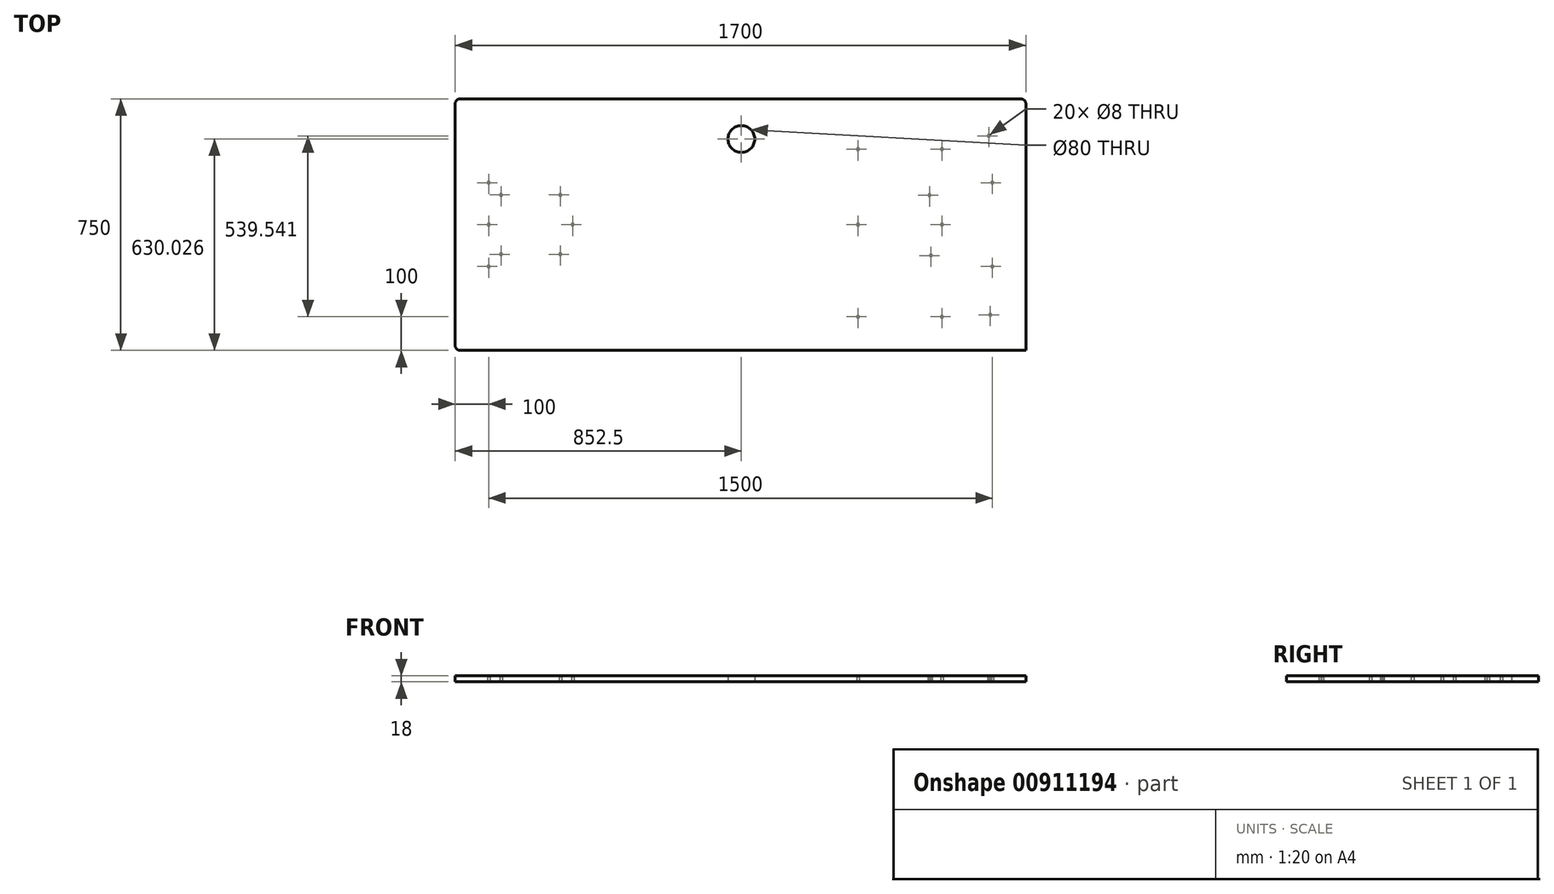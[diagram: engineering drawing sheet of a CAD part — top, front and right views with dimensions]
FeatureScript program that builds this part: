
annotation { "Feature Type Name" : "Feature", "Feature Type Description" : "" }
export const myFeature = defineFeature(function(context is Context, id is Id, definition is map)
    precondition{}
    {
        {
            var Q0;
            Q0=qCreatedBy(makeId("Top.planeOp"),FACE);
            var sketch = newSketch(context, id + "F0", { "sketchPlane" : qUnion([Q0])});
            skLineSegment(sketch, "E0", {"start": v(0, 0) * mm, "end": v(1700, 0) * mm});
            skLineSegment(sketch, "E1", {"start": v(1700, 0) * mm, "end": v(1700, -750) * mm});
            skLineSegment(sketch, "E2", {"start": v(1700, -750) * mm, "end": v(0, -750) * mm});
            skLineSegment(sketch, "E3", {"start": v(0, -750) * mm, "end": v(0, 0) * mm});
            skLineSegment(sketch, "E4", {"start": v(1700, -750) * mm, "end": v(1690, -750) * mm});
            skSolve(sketch);
        }
        {
            var Q0;
            Q0=makeQuery(id+"F0.imprint","IMPRINT",FACE,{"disambiguationData":[TD([[makeQuery(id+"F0.imprint","IMPRINT",EDGE,{"derivedFrom":sQuery(id+"F0.wireOp",EDGE,"E0")}),-1.0]])]});
            extrude(context, id + "F1", {"entities" : qUnion([Q0]), "depth" : 18 * mm, "offsetDistance" : 25 * mm});
        }
        {
            var Q0;
            Q0=makeQuery(id+"F1.opExtrude","SWEPT_EDGE",EDGE,{"disambiguationData":[OSD([sQuery(id+"F0.wireOp",EDGE,"E2"),sQuery(id+"F0.wireOp",EDGE,"E3")])]});
            var Q1;
            Q1=makeQuery(id+"F1.opExtrude","SWEPT_EDGE",EDGE,{"disambiguationData":[OSD([sQuery(id+"F0.wireOp",EDGE,"E0"),sQuery(id+"F0.wireOp",EDGE,"E3")])]});
            var Q2;
            Q2=makeQuery(id+"F1.opExtrude","SWEPT_EDGE",EDGE,{"disambiguationData":[OSD([sQuery(id+"F0.wireOp",EDGE,"E0"),sQuery(id+"F0.wireOp",EDGE,"E1")])]});
            fillet(context, id + "F2", {"entities" : qUnion([Q0, Q1, Q2]), "radius" : 15 * mm, "tangentPropagation" : true, "allowEdgeOverflow" : false});
        }
        {
            var Q0;
            Q0=makeQuery(id+"F1.opExtrude","CAP_FACE",FACE,{"disambiguationData":[OSD([sQuery(id+"F0.wireOp",EDGE,"E0"),sQuery(id+"F0.wireOp",EDGE,"E1"),sQuery(id+"F0.wireOp",EDGE,"E2"),sQuery(id+"F0.wireOp",EDGE,"E3"),sQuery(id+"F0.wireOp",EDGE,"E4")])],"isStart":true});
            var sketch = newSketch(context, id + "F3", { "sketchPlane" : qUnion([Q0])});
            skCircle(sketch, "E5", {"center": v(100, 500) * mm, "radius": 4 * mm});
            skCircle(sketch, "E6", {"center": v(100, 250) * mm, "radius": 4 * mm});
            skCircle(sketch, "E7", {"center": v(100, 375) * mm, "radius": 4 * mm});
            skCircle(sketch, "E8", {"center": v(313.39, 463.39) * mm, "radius": 4 * mm});
            skCircle(sketch, "E9", {"center": v(136.61, 286.61) * mm, "radius": 4 * mm});
            skCircle(sketch, "E10", {"center": v(136.61, 463.39) * mm, "radius": 4 * mm});
            skCircle(sketch, "E11", {"center": v(313.39, 286.61) * mm, "radius": 4 * mm});
            skCircle(sketch, "E12", {"center": v(350, 375) * mm, "radius": 4 * mm});
            skLineSegment(sketch, "E13", {"start": v(1700, 15) * mm, "end": v(1700, 115) * mm});
            skCircle(sketch, "E14", {"center": v(1450, 150) * mm, "radius": 4 * mm});
            skCircle(sketch, "E15", {"center": v(1200, 150) * mm, "radius": 4 * mm});
            skLineSegment(sketch, "E16", {"start": v(1450, 150) * mm, "end": v(1450, 0) * mm});
            skLineSegment(sketch, "E17", {"start": v(1200, 150) * mm, "end": v(1200, 0) * mm});
            skLineSegment(sketch, "E18", {"start": v(1700, 750) * mm, "end": v(1700, 375) * mm});
            skCircle(sketch, "E19", {"center": v(1450, 375) * mm, "radius": 4 * mm});
            skLineSegment(sketch, "E20", {"start": v(1450, 375) * mm, "end": v(1200, 375) * mm});
            skCircle(sketch, "E21", {"center": v(1200, 375) * mm, "radius": 4 * mm});
            skLineSegment(sketch, "E22", {"start": v(1450, 375) * mm, "end": v(1450, 650) * mm});
            skCircle(sketch, "E23", {"center": v(1450, 650) * mm, "radius": 4 * mm});
            skLineSegment(sketch, "E24", {"start": v(1450, 650) * mm, "end": v(1200, 650) * mm});
            skCircle(sketch, "E25", {"center": v(1200, 650) * mm, "radius": 4 * mm});
            skLineSegment(sketch, "E26", {"start": v(1700, 375) * mm, "end": v(1600, 375) * mm});
            skLineSegment(sketch, "E27", {"start": v(1600, 375) * mm, "end": v(1600, 250) * mm});
            skCircle(sketch, "E28", {"center": v(1600, 250) * mm, "radius": 4 * mm});
            skLineSegment(sketch, "E29", {"start": v(1600, 375) * mm, "end": v(1600, 500) * mm});
            skCircle(sketch, "E30", {"center": v(1600, 500) * mm, "radius": 4 * mm});
            skLineSegment(sketch, "E31", {"start": v(1700, 750) * mm, "end": v(1593.93, 643.93) * mm});
            skCircle(sketch, "E32", {"center": v(1593.93, 643.93) * mm, "radius": 4 * mm});
            skLineSegment(sketch, "E33", {"start": v(1593.93, 643.93) * mm, "end": v(1417.16, 467.16) * mm});
            skCircle(sketch, "E34", {"center": v(1417.16, 467.16) * mm, "radius": 4 * mm});
            skLineSegment(sketch, "E35", {"start": v(1695.6, 4.4) * mm, "end": v(1589.54, 110.46) * mm});
            skCircle(sketch, "E36", {"center": v(1589.54, 110.46) * mm, "radius": 4 * mm});
            skLineSegment(sketch, "E37", {"start": v(1589.54, 110.46) * mm, "end": v(1412.76, 287.24) * mm});
            skCircle(sketch, "E38", {"center": v(1412.76, 287.24) * mm, "radius": 4 * mm});
            skSolve(sketch);
        }
        {
            var Q0;
            Q0=sQuery(id+"F3.wireOp",VERTEX,"zo5arG6g-OJMp-sB2c-RYU5-yITN3VIuE4s3.center");
            var Q1;
            Q1=sQuery(id+"F3.wireOp",VERTEX,"MlnViuX5-Oy2d-52iN-Z55u-6jaAjh98irLr.center");
            var Q2;
            Q2=sQuery(id+"F3.wireOp",VERTEX,"bB7YACuq-bGVO-MN0k-VLhs-4qn9VgyxlBvf.center");
            var Q3;
            Q3=sQuery(id+"F3.wireOp",VERTEX,"uzjLMIpB-ZH7R-PmJq-tVHc-d7nJcNMk5Wtu.center");
            var Q4;
            Q4=sQuery(id+"F3.wireOp",VERTEX,"E9.center");
            var Q5;
            Q5=sQuery(id+"F3.wireOp",VERTEX,"E6.center");
            var Q6;
            Q6=sQuery(id+"F3.wireOp",VERTEX,"E7.center");
            var Q7;
            Q7=sQuery(id+"F3.wireOp",VERTEX,"E10.center");
            var Q8;
            Q8=sQuery(id+"F3.wireOp",VERTEX,"E5.center");
            var Q9;
            Q9=sQuery(id+"F3.wireOp",VERTEX,"E8.center");
            var Q10;
            Q10=sQuery(id+"F3.wireOp",VERTEX,"E12.center");
            var Q11;
            Q11=sQuery(id+"F3.wireOp",VERTEX,"E11.center");
            var Q12;
            Q12=sQuery(id+"F3.wireOp",VERTEX,"E15.center");
            var Q13;
            Q13=sQuery(id+"F3.wireOp",VERTEX,"E14.center");
            var Q14;
            Q14=sQuery(id+"F3.wireOp",VERTEX,"E35.end");
            var Q15;
            Q15=sQuery(id+"F3.wireOp",VERTEX,"E27.end");
            var Q16;
            Q16=sQuery(id+"F3.wireOp",VERTEX,"E20.start");
            var Q17;
            Q17=sQuery(id+"F3.wireOp",VERTEX,"E20.end");
            var Q18;
            Q18=sQuery(id+"F3.wireOp",VERTEX,"E33.end");
            var Q19;
            Q19=sQuery(id+"F3.wireOp",VERTEX,"E29.end");
            var Q20;
            Q20=sQuery(id+"F3.wireOp",VERTEX,"E31.end");
            var Q21;
            Q21=sQuery(id+"F3.wireOp",VERTEX,"E22.end");
            var Q22;
            Q22=sQuery(id+"F3.wireOp",VERTEX,"E24.end");
            var Q23;
            Q23=sQuery(id+"F3.wireOp",VERTEX,"E37.end");
            var Q24;
            Q24=makeQuery(id+"F1.opExtrude","SWEPT_BODY",BODY,{"disambiguationData":[OSD([sQuery(id+"F0.wireOp",EDGE,"E0"),sQuery(id+"F0.wireOp",EDGE,"E1"),sQuery(id+"F0.wireOp",EDGE,"E2"),sQuery(id+"F0.wireOp",EDGE,"E3"),sQuery(id+"F0.wireOp",EDGE,"E4")])]});
            hole(context, id + "F4", {"style" : HoleStyle.SIMPLE, "endStyle" : HoleEndStyle.BLIND, "holeDiameter" : 8 * mm, "majorDiameter" : 5 * mm, "holeDepth" : 15 * mm, "isTappedThrough" : true, "tappedDepth" : 12 * mm, "tapClearance" : 3, "locations" : qUnion([Q0, Q1, Q2, Q3, Q4, Q5, Q6, Q7, Q8, Q9, Q10, Q11, Q12, Q13, Q14, Q15, Q16, Q17, Q18, Q19, Q20, Q21, Q22, Q23]), "scope" : qUnion([Q24])});
        }
        {
            var Q0;
            Q0=makeQuery(id+"F1.opExtrude","CAP_FACE",FACE,{"disambiguationData":[OSD([sQuery(id+"F0.wireOp",EDGE,"E0"),sQuery(id+"F0.wireOp",EDGE,"E1"),sQuery(id+"F0.wireOp",EDGE,"E2"),sQuery(id+"F0.wireOp",EDGE,"E3"),sQuery(id+"F0.wireOp",EDGE,"E4")])],"isStart":true});
            var sketch = newSketch(context, id + "F5", { "sketchPlane" : qUnion([Q0])});
            skLineSegment(sketch, "E39", {"start": v(1700, 750) * mm, "end": v(857.5, 750) * mm});
            skLineSegment(sketch, "E40", {"start": v(850, 0) * mm, "end": v(852.5, 119.97) * mm});
            skCircle(sketch, "E41", {"center": v(852.5, 119.97) * mm, "radius": 40 * mm});
            skSolve(sketch);
        }
        {
            var Q0;
            Q0 = qSketchRegion(id + "F5", true);
            extrude(context, id + "F6", {"entities" : qUnion([Q0]), "operationType" : NewBodyOperationType.REMOVE, "oppositeDirection" : true, "depth" : 18 * mm, "offsetDistance" : 25 * mm});
        }
    });
